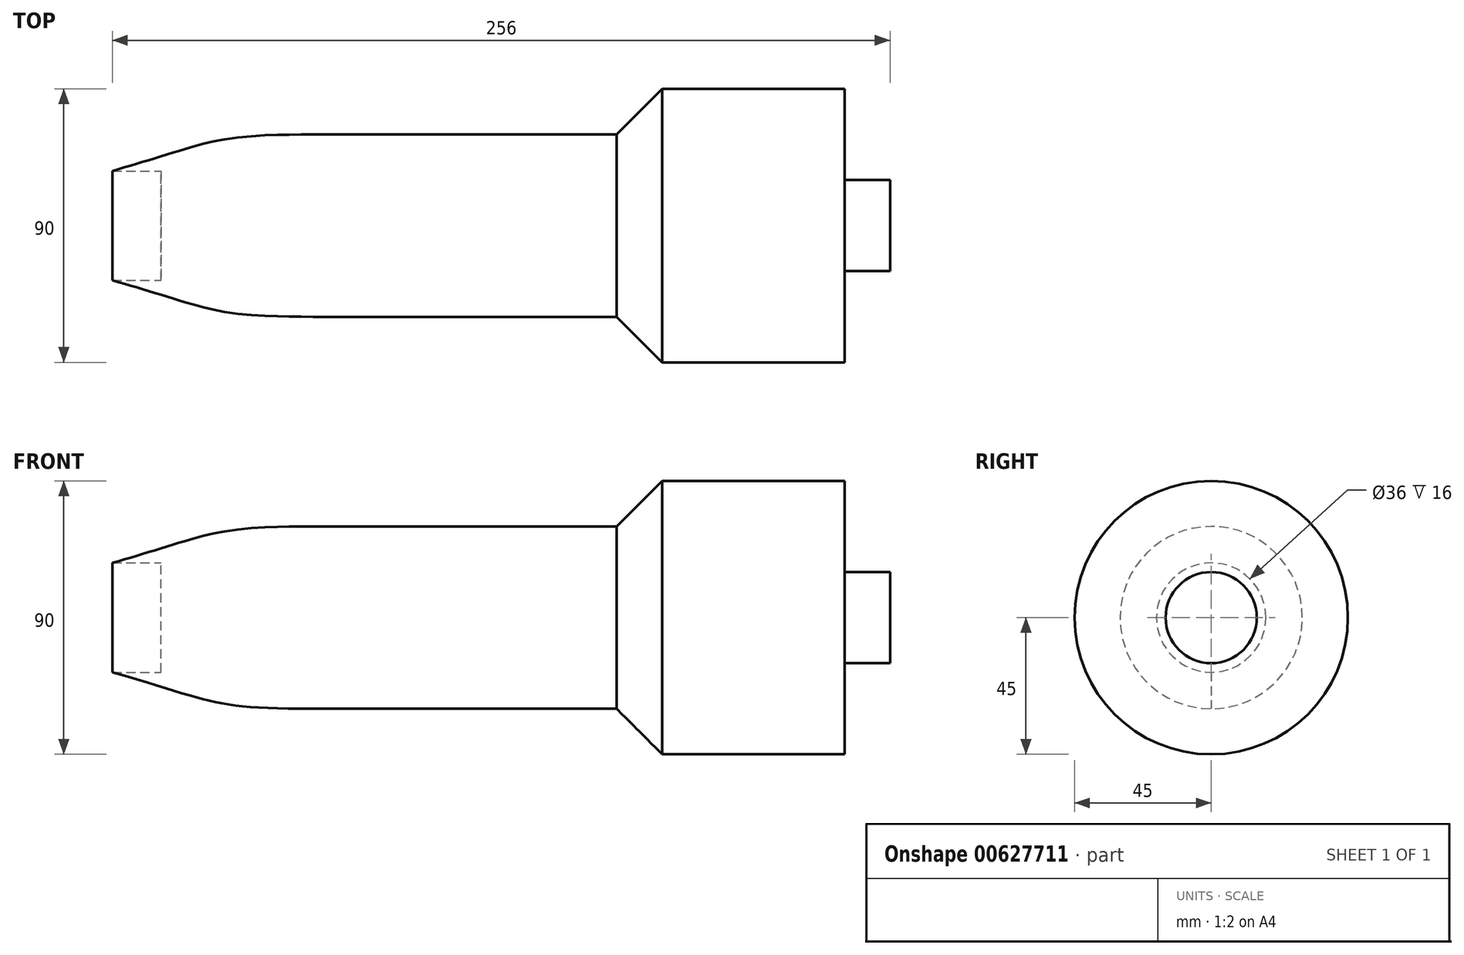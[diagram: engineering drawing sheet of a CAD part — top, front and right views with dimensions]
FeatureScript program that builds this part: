
annotation { "Feature Type Name" : "Feature", "Feature Type Description" : "" }
export const myFeature = defineFeature(function(context is Context, id is Id, definition is map)
    precondition{}
    {
        {
            var Q0;
            Q0=qCreatedBy(makeId("Front.planeOp"),FACE);
            var sketch = newSketch(context, id + "F0", { "sketchPlane" : qUnion([Q0])});
            skLineSegment(sketch, "E0", {"start": v(0, 0) * mm, "end": v(0, 18) * mm});
            skLineSegment(sketch, "E1", {"start": v(0, 18) * mm, "end": v(-16, 18) * mm});
            skLineSegment(sketch, "E2", {"start": v(50, 0) * mm, "end": v(0, 0) * mm});
            skLineSegment(sketch, "E3", {"start": v(50, 0) * mm, "end": v(50, 30) * mm});
            skFitSpline(sketch, "E4", {"points": [v(-16, 18) * mm, v(50, 30) * mm], "startDerivative": vector(99.96, 28.56) * mm, "endDerivative": vector(101.55, 0) * mm});
            skLineSegment(sketch, "E5", {"start": v(50, 30) * mm, "end": v(0, 30) * mm});
            skLineSegment(sketch, "E6", {"start": v(50, 0) * mm, "end": v(150, 0) * mm});
            skLineSegment(sketch, "E7", {"start": v(50, 30) * mm, "end": v(150, 30) * mm});
            skLineSegment(sketch, "E8", {"start": v(150, 0) * mm, "end": v(150, 30) * mm});
            skSolve(sketch);
        }
        {
            var Q0;
            Q0=makeQuery(id+"F0.imprint","IMPRINT",FACE,{"disambiguationData":[TD([[makeQuery(id+"F0.imprint","IMPRINT",EDGE,{"derivedFrom":sQuery(id+"F0.wireOp",EDGE,"E0")}),-1.0]])]});
            var Q1;
            Q1=makeQuery(id+"F0.imprint","IMPRINT",FACE,{"disambiguationData":[TD([[makeQuery(id+"F0.imprint","IMPRINT",EDGE,{"derivedFrom":sQuery(id+"F0.wireOp",EDGE,"E3")}),-1.0]])]});
            var Q2;
            Q2=sQuery(id+"F0.wireOp",EDGE,"E2");
            revolve(context, id + "F1", {"entities" : qUnion([Q0, Q1]), "axis" : qUnion([Q2]), "revolveType" : RevolveType.FULL});
        }
        {
            var Q0;
            Q0=qCreatedBy(makeId("Right.planeOp"),FACE);
            cPlane(context, id + "F2", {"entities" : qUnion([Q0]), "cplaneType" : CPlaneType.OFFSET, "offset" : 150 * mm, "width" : 150 * mm, "height" : 150 * mm});
        }
        {
            var Q0;
            Q0=qCreatedBy(id+"F2.planeOp",FACE);
            var sketch = newSketch(context, id + "F3", { "sketchPlane" : qUnion([Q0])});
            skCircle(sketch, "E9", {"center": v(0, 0) * mm, "radius": 30 * mm});
            skCircle(sketch, "E10", {"center": v(0, 0) * mm, "radius": 45 * mm});
            skSolve(sketch);
        }
        {
            var Q0;
            Q0 = qSketchRegion(id + "F3", true);
            var Q1;
            Q1=makeQuery(id+"F3.imprint","IMPRINT",FACE,{"disambiguationData":[TD([[makeQuery(id+"F3.imprint","IMPRINT",EDGE,{"derivedFrom":sQuery(id+"F3.wireOp",EDGE,"E9")}),1.0]])]});
            extrude(context, id + "F4", {"entities" : qUnion([Q0, Q1]), "operationType" : NewBodyOperationType.ADD, "depth" : 75 * mm, "offsetDistance" : 25 * mm});
        }
        {
            var Q0;
            Q0=makeQuery(id+"F4.opExtrude","CAP_EDGE",EDGE,{"disambiguationData":[OSD([sQuery(id+"F3.wireOp",EDGE,"E10")])],"isStart":true});
            chamfer(context, id + "F5", {"entities" : qUnion([Q0]), "width" : 15 * mm, "tangentPropagation" : true});
        }
        {
            var Q0;
            Q0=qCreatedBy(id+"F2.planeOp",FACE);
            cPlane(context, id + "F6", {"entities" : qUnion([Q0]), "cplaneType" : CPlaneType.OFFSET, "offset" : 75 * mm, "width" : 150 * mm, "height" : 150 * mm});
        }
        {
            var Q0;
            Q0=qCreatedBy(id+"F6.planeOp",FACE);
            var sketch = newSketch(context, id + "F7", { "sketchPlane" : qUnion([Q0])});
            skCircle(sketch, "E11", {"center": v(0, 0) * mm, "radius": 15 * mm});
            skSolve(sketch);
        }
        {
            var Q0;
            Q0 = qSketchRegion(id + "F7", true);
            extrude(context, id + "F8", {"entities" : qUnion([Q0]), "operationType" : NewBodyOperationType.ADD, "depth" : 15 * mm, "offsetDistance" : 25 * mm});
        }
    });
